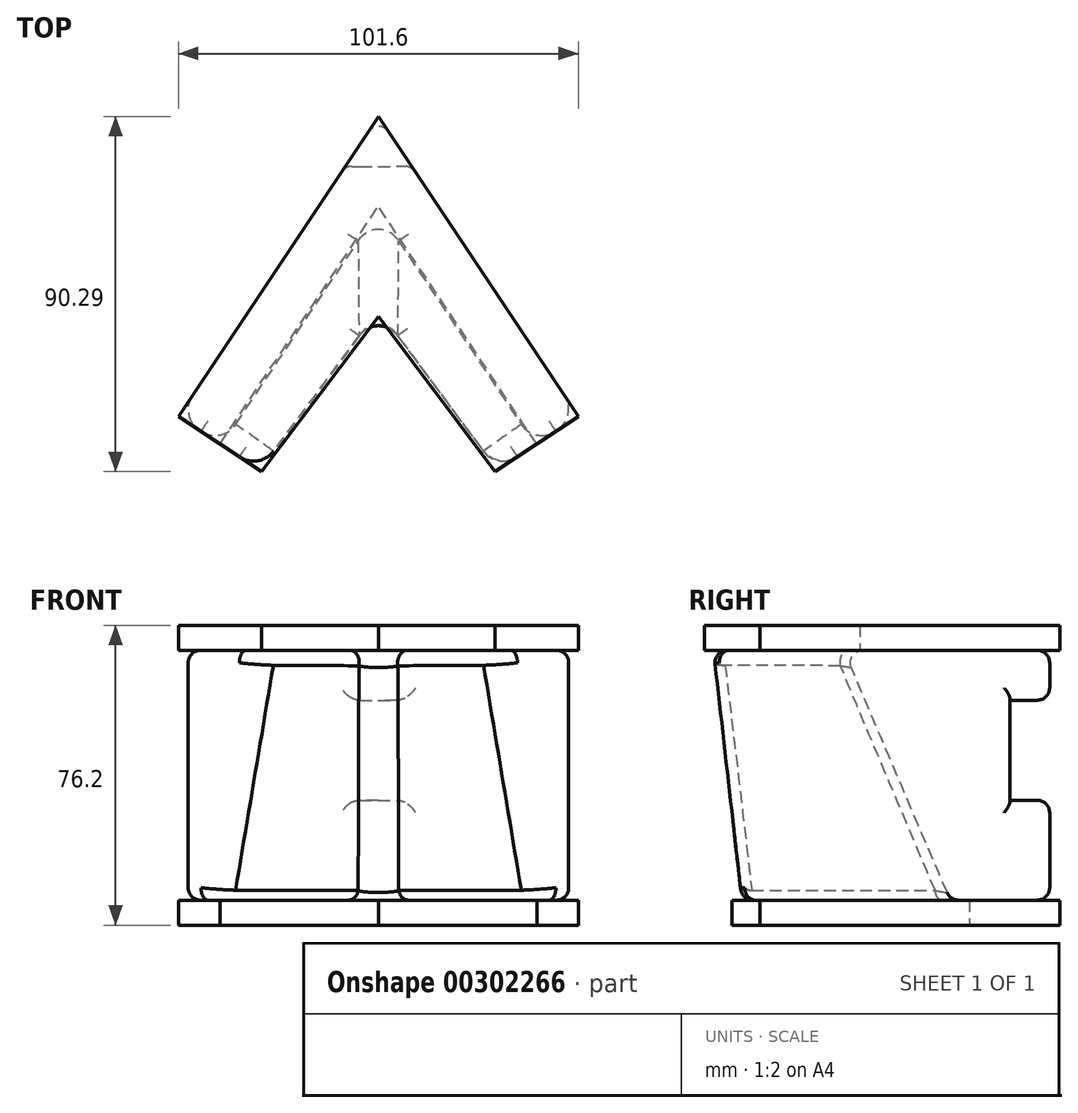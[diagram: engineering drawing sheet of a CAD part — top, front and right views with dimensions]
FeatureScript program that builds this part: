
annotation { "Feature Type Name" : "Feature", "Feature Type Description" : "" }
export const myFeature = defineFeature(function(context is Context, id is Id, definition is map)
    precondition{}
    {
        {
            var Q0;
            Q0=qCreatedBy(makeId("Top.planeOp"),FACE);
            var sketch = newSketch(context, id + "F0", { "sketchPlane" : qUnion([Q0])});
            skLineSegment(sketch, "E0", {"start": v(0, 76.2) * mm, "end": v(-50.8, 0) * mm});
            skLineSegment(sketch, "E1", {"start": v(0, 76.2) * mm, "end": v(50.8, 0) * mm});
            skLineSegment(sketch, "E2", {"start": v(-50.8, 0) * mm, "end": v(-40.23, -7.04) * mm});
            skLineSegment(sketch, "E3", {"start": v(-40.23, -7.04) * mm, "end": v(0, 53.3) * mm});
            skLineSegment(sketch, "E4", {"start": v(50.8, 0) * mm, "end": v(40.23, -7.04) * mm});
            skLineSegment(sketch, "E5", {"start": v(40.23, -7.04) * mm, "end": v(0, 53.3) * mm});
            skSolve(sketch);
        }
        {
            var Q0;
            Q0 = qSketchRegion(id + "F0", true);
            extrude(context, id + "F1", {"entities" : qUnion([Q0]), "depth" : 6.35 * mm});
        }
        {
            var Q0;
            Q0=qCreatedBy(makeId("Top.planeOp"),FACE);
            var sketch = newSketch(context, id + "F2", { "sketchPlane" : qUnion([Q0])});
            skLineSegment(sketch, "E6", {"start": v(0, 76.2) * mm, "end": v(-50.8, 0) * mm});
            skLineSegment(sketch, "E7", {"start": v(-50.8, 0) * mm, "end": v(-29.67, -14.09) * mm});
            skLineSegment(sketch, "E8", {"start": v(0, 76.2) * mm, "end": v(50.8, 0) * mm});
            skLineSegment(sketch, "E9", {"start": v(50.8, 0) * mm, "end": v(29.67, -14.09) * mm});
            skLineSegment(sketch, "E10", {"start": v(-29.67, -14.09) * mm, "end": v(0, 25.4) * mm});
            skLineSegment(sketch, "E11", {"start": v(0, 25.4) * mm, "end": v(29.67, -14.09) * mm});
            skSolve(sketch);
        }
        {
            var Q0;
            Q0 = qSketchRegion(id + "F2", true);
            extrude(context, id + "F3", {"entities" : qUnion([Q0]), "depth" : 76.2 * mm, "hasSecondDirection" : true, "secondDirectionOppositeDirection" : false, "secondDirectionDepth" : 69.85 * mm});
        }
        {
            var Q0;
            Q0=makeQuery(id+"F3.opExtrude","CAP_FACE",FACE,{"disambiguationData":[OSD([sQuery(id+"F2.wireOp",EDGE,"E6"),sQuery(id+"F2.wireOp",EDGE,"E7"),sQuery(id+"F2.wireOp",EDGE,"E8"),sQuery(id+"F2.wireOp",EDGE,"E9"),sQuery(id+"F2.wireOp",EDGE,"E10"),sQuery(id+"F2.wireOp",EDGE,"E11")])],"isStart":true});
            var Q1;
            Q1=makeQuery(id+"F1.opExtrude","CAP_FACE",FACE,{"disambiguationData":[OSD([sQuery(id+"F0.wireOp",EDGE,"E0"),sQuery(id+"F0.wireOp",EDGE,"E1"),sQuery(id+"F0.wireOp",EDGE,"E2"),sQuery(id+"F0.wireOp",EDGE,"E3"),sQuery(id+"F0.wireOp",EDGE,"E4"),sQuery(id+"F0.wireOp",EDGE,"E5")])],"isStart":false});
            loft(context, id + "F4", {"sheetProfilesArray" : [{ "sheetProfileEntities" : qUnion([Q0]) }, { "sheetProfileEntities" : qUnion([Q1]) }]});
        }
        {
            var Q0;
            Q0=qCreatedBy(makeId("Right.planeOp"),FACE);
            var sketch = newSketch(context, id + "F5", { "sketchPlane" : qUnion([Q0])});
            skLineSegment(sketch, "E12", {"start": v(76.2, 31.75) * mm, "end": v(76.2, 57.15) * mm});
            skLineSegment(sketch, "E13", {"start": v(76.2, 31.75) * mm, "end": v(63.5, 31.75) * mm});
            skLineSegment(sketch, "E14", {"start": v(63.5, 31.75) * mm, "end": v(63.5, 57.15) * mm});
            skLineSegment(sketch, "E15", {"start": v(63.5, 57.15) * mm, "end": v(76.2, 57.15) * mm});
            skSolve(sketch);
        }
        {
            var Q0;
            Q0 = qSketchRegion(id + "F5", true);
            extrude(context, id + "F6", {"entities" : qUnion([Q0]), "operationType" : NewBodyOperationType.REMOVE, "oppositeDirection" : true, "depth" : 25.4 * mm, "hasSecondDirection" : true, "secondDirectionOppositeDirection" : false, "secondDirectionDepth" : 25.4 * mm});
        }
        {
            var Q0;
            Q0=makeQuery(id+"F4.opLoft","SWEPT_EDGE",EDGE,{"disambiguationData":[OSD([sQuery(id+"F0.wireOp",EDGE,"E4"),sQuery(id+"F0.wireOp",EDGE,"E5"),sQuery(id+"F2.wireOp",EDGE,"E9"),sQuery(id+"F2.wireOp",EDGE,"E11")])]});
            var Q1;
            Q1=makeQuery(id+"F4.opLoft","SWEPT_EDGE",EDGE,{"disambiguationData":[OSD([sQuery(id+"F0.wireOp",EDGE,"E1"),sQuery(id+"F0.wireOp",EDGE,"E4"),sQuery(id+"F2.wireOp",EDGE,"E8"),sQuery(id+"F2.wireOp",EDGE,"E9")])]});
            var Q2;
            Q2=makeQuery(id+"F4.opLoft","SWEPT_EDGE",EDGE,{"disambiguationData":[OSD([sQuery(id+"F0.wireOp",EDGE,"E2"),sQuery(id+"F0.wireOp",EDGE,"E3"),sQuery(id+"F2.wireOp",EDGE,"E7"),sQuery(id+"F2.wireOp",EDGE,"E10")])]});
            var Q3;
            Q3=makeQuery(id+"F4.opLoft","SWEPT_EDGE",EDGE,{"disambiguationData":[OSD([sQuery(id+"F0.wireOp",EDGE,"E0"),sQuery(id+"F0.wireOp",EDGE,"E2"),sQuery(id+"F2.wireOp",EDGE,"E6"),sQuery(id+"F2.wireOp",EDGE,"E7")])]});
            var Q4;
            Q4=makeQuery(id+"F4.opLoft","SWEPT_EDGE",EDGE,{"disambiguationData":[OSD([sQuery(id+"F0.wireOp",EDGE,"E3"),sQuery(id+"F0.wireOp",EDGE,"E5"),sQuery(id+"F2.wireOp",EDGE,"E10"),sQuery(id+"F2.wireOp",EDGE,"E11")])]});
            fillet(context, id + "F7", {"entities" : qUnion([Q0, Q1, Q2, Q3, Q4]), "radius" : 6.35 * mm, "tangentPropagation" : true, "allowEdgeOverflow" : false});
        }
        {
            var Q0;
            Q0=makeQuery(id+"F4.opLoft","SWEPT_FACE",FACE,{"disambiguationData":[OSD([sQuery(id+"F0.wireOp",EDGE,"E0"),sQuery(id+"F0.wireOp",EDGE,"E1"),sQuery(id+"F0.wireOp",EDGE,"E4"),sQuery(id+"F2.wireOp",EDGE,"E6"),sQuery(id+"F2.wireOp",EDGE,"E8"),sQuery(id+"F2.wireOp",EDGE,"E9")])]});
            var Q1;
            Q1=makeQuery(id+"F6.boolean.opBoolean","INTERSECT",EDGE,{"derivedFrom":[makeQuery(id+"F4.opLoft","SWEPT_FACE",FACE,{"disambiguationData":[OSD([sQuery(id+"F0.wireOp",EDGE,"E0"),sQuery(id+"F0.wireOp",EDGE,"E1"),sQuery(id+"F0.wireOp",EDGE,"E2"),sQuery(id+"F2.wireOp",EDGE,"E6"),sQuery(id+"F2.wireOp",EDGE,"E7"),sQuery(id+"F2.wireOp",EDGE,"E8")])]}),makeQuery(id+"F6.opExtrude","SWEPT_FACE",FACE,{"disambiguationData":[OSD([sQuery(id+"F5.wireOp",EDGE,"E13")])]})]});
            var Q2;
            Q2=makeQuery(id+"F6.boolean.opBoolean","INTERSECT",EDGE,{"derivedFrom":[makeQuery(id+"F4.opLoft","SWEPT_FACE",FACE,{"disambiguationData":[OSD([sQuery(id+"F0.wireOp",EDGE,"E0"),sQuery(id+"F0.wireOp",EDGE,"E1"),sQuery(id+"F0.wireOp",EDGE,"E2"),sQuery(id+"F2.wireOp",EDGE,"E6"),sQuery(id+"F2.wireOp",EDGE,"E7"),sQuery(id+"F2.wireOp",EDGE,"E8")])]}),makeQuery(id+"F6.opExtrude","SWEPT_FACE",FACE,{"disambiguationData":[OSD([sQuery(id+"F5.wireOp",EDGE,"E14")])]})]});
            var Q3;
            Q3=makeQuery(id+"F6.boolean.opBoolean","INTERSECT",EDGE,{"derivedFrom":[makeQuery(id+"F4.opLoft","SWEPT_FACE",FACE,{"disambiguationData":[OSD([sQuery(id+"F0.wireOp",EDGE,"E0"),sQuery(id+"F0.wireOp",EDGE,"E1"),sQuery(id+"F0.wireOp",EDGE,"E2"),sQuery(id+"F2.wireOp",EDGE,"E6"),sQuery(id+"F2.wireOp",EDGE,"E7"),sQuery(id+"F2.wireOp",EDGE,"E8")])]}),makeQuery(id+"F6.opExtrude","SWEPT_FACE",FACE,{"disambiguationData":[OSD([sQuery(id+"F5.wireOp",EDGE,"E15")])]})]});
            var Q4;
            Q4=makeQuery(id+"F4.opLoft","MID_CAP_EDGE",EDGE,{"disambiguationData":[OSD([sQuery(id+"F0.wireOp",EDGE,"E0"),sQuery(id+"F0.wireOp",EDGE,"E1"),sQuery(id+"F0.wireOp",EDGE,"E2")])],"capPos":1.0});
            var Q5;
            Q5=makeQuery(id+"F4.opLoft","MID_CAP_EDGE",EDGE,{"disambiguationData":[OSD([sQuery(id+"F2.wireOp",EDGE,"E6"),sQuery(id+"F2.wireOp",EDGE,"E7"),sQuery(id+"F2.wireOp",EDGE,"E8")])],"capPos":0.0});
            var Q6;
            Q6=makeQuery(id+"F4.opLoft","MID_CAP_EDGE",EDGE,{"disambiguationData":[OSD([sQuery(id+"F0.wireOp",EDGE,"E2"),sQuery(id+"F0.wireOp",EDGE,"E3"),sQuery(id+"F0.wireOp",EDGE,"E5")])],"capPos":1.0});
            var Q7;
            Q7=makeQuery(id+"F4.opLoft","MID_CAP_EDGE",EDGE,{"disambiguationData":[OSD([sQuery(id+"F2.wireOp",EDGE,"E7"),sQuery(id+"F2.wireOp",EDGE,"E10"),sQuery(id+"F2.wireOp",EDGE,"E11")])],"capPos":0.0});
            var Q8;
            Q8=makeQuery(id+"F4.opLoft","MID_CAP_EDGE",EDGE,{"disambiguationData":[OSD([sQuery(id+"F2.wireOp",EDGE,"E6"),sQuery(id+"F2.wireOp",EDGE,"E7"),sQuery(id+"F2.wireOp",EDGE,"E10")])],"capPos":0.0});
            var Q9;
            {var subQ0=sQuery(id+"F0.wireOp",EDGE,"E3");var subQ1=sQuery(id+"F0.wireOp",EDGE,"E2");Q9=makeQuery(id+"F7.opFillet","BLEND_EDGE",EDGE,{"blendedFrom":[makeQuery(id+"F4.opLoft","SWEPT_EDGE",EDGE,{"disambiguationData":[OSD([subQ1,subQ0,sQuery(id+"F2.wireOp",EDGE,"E7"),sQuery(id+"F2.wireOp",EDGE,"E10")])]}),makeQuery(id+"F4.opLoft","CAP_FACE",FACE,{"disambiguationData":[OSD([sQuery(id+"F0.wireOp",EDGE,"E0"),sQuery(id+"F0.wireOp",EDGE,"E1"),subQ1,subQ0,sQuery(id+"F0.wireOp",EDGE,"E4"),sQuery(id+"F0.wireOp",EDGE,"E5")])],"isStart":true})],"blendedInto":[makeQuery(id+"F4.opLoft","CAP_FACE",FACE,{"disambiguationData":[OSD([sQuery(id+"F0.wireOp",EDGE,"E0"),sQuery(id+"F0.wireOp",EDGE,"E1"),subQ1,subQ0,sQuery(id+"F0.wireOp",EDGE,"E4"),sQuery(id+"F0.wireOp",EDGE,"E5")])],"isStart":true})]});}
            fillet(context, id + "F8", {"entities" : qUnion([Q0, Q1, Q2, Q3, Q4, Q5, Q6, Q7, Q8, Q9]), "radius" : 3.17 * mm, "allowEdgeOverflow" : false});
        }
    });
